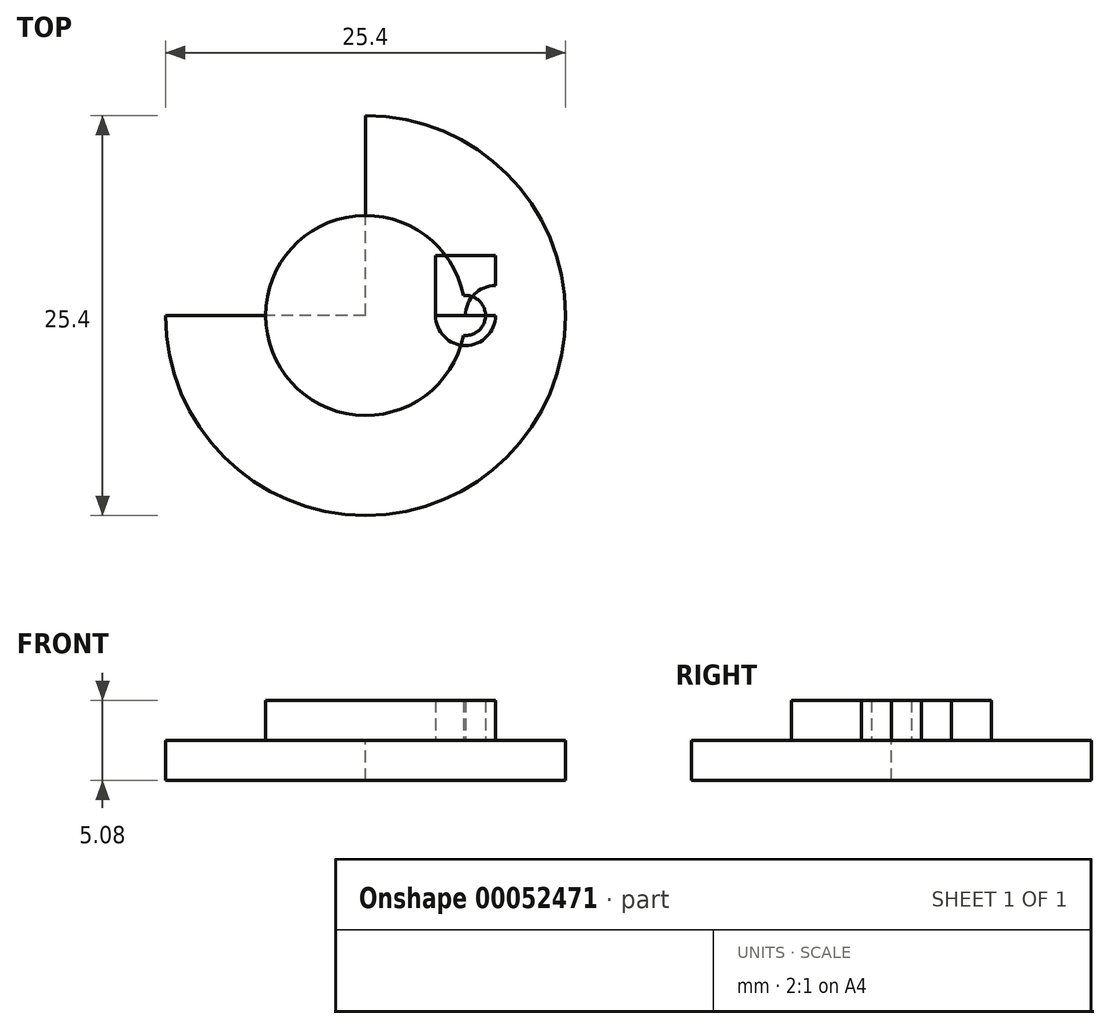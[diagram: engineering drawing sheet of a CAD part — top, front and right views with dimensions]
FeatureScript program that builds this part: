
annotation { "Feature Type Name" : "Feature", "Feature Type Description" : "" }
export const myFeature = defineFeature(function(context is Context, id is Id, definition is map)
    precondition{}
    {
        {
            var Q0;
            Q0=qCreatedBy(makeId("Top.planeOp"),FACE);
            var sketch = newSketch(context, id + "F0", { "sketchPlane" : qUnion([Q0])});
            skArc(sketch, "E0", {"start": v(-12.7, 0) * mm, "mid": v(8.98, -8.98) * mm, "end": v(0, 12.7) * mm});
            skLineSegment(sketch, "E1.bottom", {"start": v(0, 0) * mm, "end": v(-12.7, 0) * mm});
            skLineSegment(sketch, "E1.left", {"start": v(0, 0) * mm, "end": v(0, 12.7) * mm});
            skSolve(sketch);
        }
        {
            var Q0;
            Q0 = qSketchRegion(id + "F0", true);
            extrude(context, id + "F1", {"entities" : qUnion([Q0]), "oppositeDirection" : true, "depth" : 2.54 * mm});
        }
        {
            var Q0;
            Q0=qCreatedBy(makeId("Top.planeOp"),FACE);
            var sketch = newSketch(context, id + "F2", { "sketchPlane" : qUnion([Q0])});
            skArc(sketch, "E2", {"start": v(6.22, 1.26) * mm, "mid": v(-6.35, 0) * mm, "end": v(6.22, -1.26) * mm});
            skArc(sketch, "E3", {"start": v(6.22, -1.26) * mm, "mid": v(7.62, 0) * mm, "end": v(6.22, 1.26) * mm});
            skSolve(sketch);
        }
        {
            var Q0;
            Q0 = qSketchRegion(id + "F2", true);
            extrude(context, id + "F3", {"entities" : qUnion([Q0]), "depth" : 2.54 * mm});
        }
        {
            var Q0;
            Q0=qCreatedBy(makeId("Top.planeOp"),FACE);
            var sketch = newSketch(context, id + "F4", { "sketchPlane" : qUnion([Q0])});
            skArc(sketch, "E4", {"start": v(4.45, 0) * mm, "mid": v(6.35, -1.9) * mm, "end": v(8.26, 0) * mm});
            skLineSegment(sketch, "E5", {"start": v(8.26, 0) * mm, "end": v(4.45, 0) * mm});
            skSolve(sketch);
        }
        {
            var Q0;
            Q0 = qSketchRegion(id + "F4", true);
            extrude(context, id + "F5", {"entities" : qUnion([Q0]), "depth" : 2.54 * mm});
        }
        {
            var Q0;
            Q0=qCreatedBy(makeId("Top.planeOp"),FACE);
            var sketch = newSketch(context, id + "F6", { "sketchPlane" : qUnion([Q0])});
            skLineSegment(sketch, "E6.bottom", {"start": v(4.45, 0) * mm, "end": v(6.35, 0) * mm});
            skLineSegment(sketch, "E6.top", {"start": v(4.45, 3.8) * mm, "end": v(8.26, 3.8) * mm});
            skLineSegment(sketch, "E6.left", {"start": v(4.45, 0) * mm, "end": v(4.45, 3.8) * mm});
            skLineSegment(sketch, "E6.right", {"start": v(8.26, 1.9) * mm, "end": v(8.26, 3.8) * mm});
            skArc(sketch, "E7", {"start": v(8.26, 1.9) * mm, "mid": v(6.9, 1.35) * mm, "end": v(6.35, 0) * mm});
            skSolve(sketch);
        }
        {
            var Q0;
            Q0=makeQuery(id+"F6.imprint","IMPRINT",FACE,{"disambiguationData":[TD([[makeQuery(id+"F6.imprint","IMPRINT",EDGE,{"derivedFrom":sQuery(id+"F6.wireOp",EDGE,"E6.bottom")}),1.0]])]});
            extrude(context, id + "F7", {"entities" : qUnion([Q0]), "depth" : 2.54 * mm});
        }
    });
